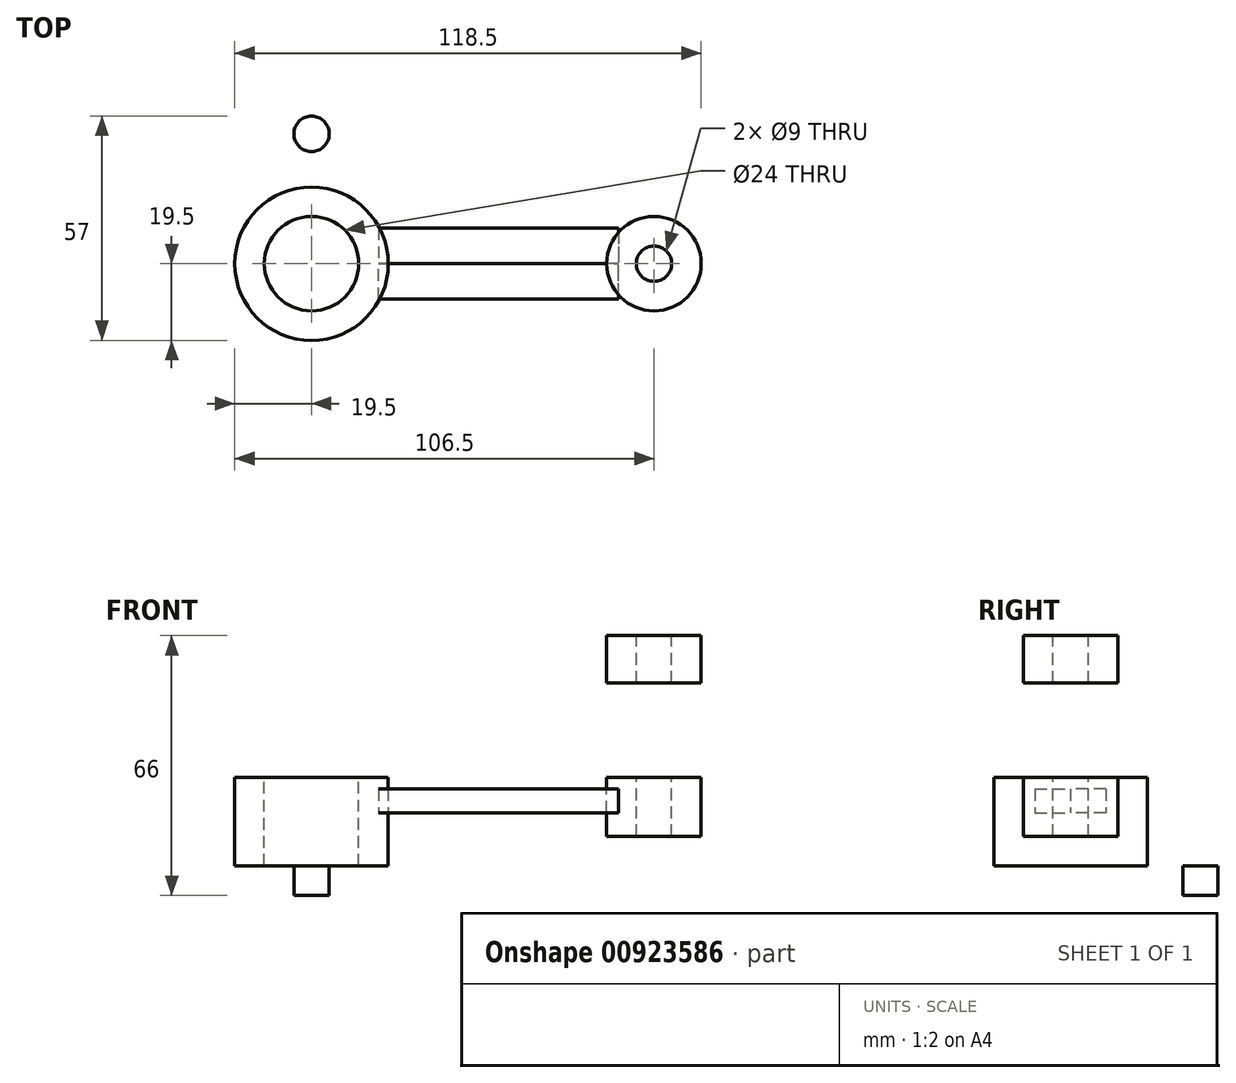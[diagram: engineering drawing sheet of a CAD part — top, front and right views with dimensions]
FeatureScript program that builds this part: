
annotation { "Feature Type Name" : "Feature", "Feature Type Description" : "" }
export const myFeature = defineFeature(function(context is Context, id is Id, definition is map)
    precondition{}
    {
        {
            var Q0;
            Q0=qCreatedBy(makeId("Top.planeOp"),FACE);
            var sketch = newSketch(context, id + "F0", { "sketchPlane" : qUnion([Q0])});
            skLineSegment(sketch, "E0.bottom", {"start": v(19.5, 45) * mm, "end": v(-19.5, 45) * mm});
            skLineSegment(sketch, "E0.top", {"start": v(19.5, -45) * mm, "end": v(-19.5, -45) * mm});
            skLineSegment(sketch, "E0.left", {"start": v(19.5, 45) * mm, "end": v(19.5, -45) * mm});
            skLineSegment(sketch, "E0.right", {"start": v(-19.5, 45) * mm, "end": v(-19.5, -45) * mm});
            skPoint(sketch, "E0.middle", {"position": v(0, 0) * mm});
            skSolve(sketch);
        }
        {
            var Q0;
            Q0=makeQuery(id+"F0.imprint","IMPRINT",FACE,{"disambiguationData":[TD([[makeQuery(id+"F0.imprint","IMPRINT",EDGE,{"derivedFrom":sQuery(id+"F0.wireOp",EDGE,"E0.bottom")}),1.0]])]});
            extrude(context, id + "F1", {"entities" : qUnion([Q0]), "depth" : 7.5 * mm, "offsetDistance" : 25 * mm});
        }
        {
            var Q0;
            Q0=makeQuery(id+"F1.opExtrude","CAP_FACE",FACE,{"disambiguationData":[OSD([sQuery(id+"F0.wireOp",EDGE,"E0.bottom"),sQuery(id+"F0.wireOp",EDGE,"E0.top"),sQuery(id+"F0.wireOp",EDGE,"E0.left"),sQuery(id+"F0.wireOp",EDGE,"E0.right")])],"isStart":false});
            var sketch = newSketch(context, id + "F2", { "sketchPlane" : qUnion([Q0])});
            skCircle(sketch, "E1", {"center": v(0, 0) * mm, "radius": 19.5 * mm});
            skSolve(sketch);
        }
        {
            var Q0;
            {var subQ0=sQuery(id+"F0.wireOp",EDGE,"E0.right");var subQ1=sQuery(id+"F0.wireOp",EDGE,"E0.left");var subQ2=sQuery(id+"F0.wireOp",EDGE,"E0.top");var subQ3=makeQuery(id+"F1.opExtrude","CAP_FACE",FACE,{"disambiguationData":[OSD([sQuery(id+"F0.wireOp",EDGE,"E0.bottom"),subQ2,subQ1,subQ0])],"isStart":false});Q0=makeQuery(id+"FBpe31tHuC7by74_1.boolean.opBoolean","SPLIT",FACE,{"disambiguationData":[TD([makeQuery(id+"F1.opExtrude","SWEPT_FACE",FACE,{"disambiguationData":[OSD([subQ2])]})])],"derivedFrom":subQ3});}
            var sketch = newSketch(context, id + "F3", { "sketchPlane" : qUnion([Q0])});
            skCircle(sketch, "E2", {"center": v(0, -33) * mm, "radius": 4.5 * mm});
            skCircle(sketch, "E3.MirrorC", {"center": v(0, 33) * mm, "radius": 4.5 * mm});
            skSolve(sketch);
        }
        {
            var Q0;
            Q0=makeQuery(id+"F3.imprint","IMPRINT",FACE,{"disambiguationData":[TD([[makeQuery(id+"F3.imprint","IMPRINT",EDGE,{"derivedFrom":sQuery(id+"F3.wireOp",EDGE,"E2")}),1.0]])]});
            var Q1;
            Q1=makeQuery(id+"F3.imprint","IMPRINT",FACE,{"disambiguationData":[TD([[makeQuery(id+"F3.imprint","IMPRINT",EDGE,{"derivedFrom":sQuery(id+"F3.wireOp",EDGE,"E3.MirrorC")}),-1.0]])]});
            var Q2;
            Q2=makeQuery(id+"F1.opExtrude","CAP_FACE",FACE,{"disambiguationData":[OSD([sQuery(id+"F0.wireOp",EDGE,"E0.bottom"),sQuery(id+"F0.wireOp",EDGE,"E0.top"),sQuery(id+"F0.wireOp",EDGE,"E0.left"),sQuery(id+"F0.wireOp",EDGE,"E0.right")])],"isStart":true});
            extrude(context, id + "F4", {"entities" : qUnion([Q0, Q1]), "operationType" : NewBodyOperationType.REMOVE, "endBound" : BoundingType.UP_TO_SURFACE, "oppositeDirection" : true, "depth" : 25 * mm, "endBoundEntityFace" : qUnion([Q2]), "offsetDistance" : 25 * mm});
        }
        {
            var Q0;
            {var subQ0=sQuery(id+"F2.wireOp",EDGE,"E1");var subQ1=makeQuery(id+"F2.imprint","INTERSECT",VERTEX,{"derivedFrom":[makeQuery(id+"F1.opExtrude","CAP_EDGE",EDGE,{"disambiguationData":[OSD([sQuery(id+"F0.wireOp",EDGE,"E0.left")])],"isStart":false}),subQ0]});Q0=makeQuery(id+"F2.imprint","IMPRINT",FACE,{"disambiguationData":[TD([[makeQuery(id+"F2.imprint","IMPRINT",EDGE,{"disambiguationData":[TD([[subQ1,-1.0]])],"derivedFrom":subQ0}),1.0]])]});}
            extrude(context, id + "F5", {"entities" : qUnion([Q0]), "operationType" : NewBodyOperationType.ADD, "depth" : 22.5 * mm, "offsetDistance" : 25 * mm});
        }
        {
            var Q0;
            Q0=makeQuery(id+"F5.opExtrude","CAP_FACE",FACE,{"disambiguationData":[OSD([sQuery(id+"F2.wireOp",EDGE,"E1")])],"isStart":false});
            var sketch = newSketch(context, id + "F6", { "sketchPlane" : qUnion([Q0])});
            skCircle(sketch, "E4", {"center": v(0, 0) * mm, "radius": 12 * mm});
            skSolve(sketch);
        }
        {
            var Q0;
            Q0=makeQuery(id+"F6.imprint","IMPRINT",FACE,{"disambiguationData":[TD([[makeQuery(id+"F6.imprint","IMPRINT",EDGE,{"derivedFrom":sQuery(id+"F6.wireOp",EDGE,"E4")}),1.0]])]});
            var Q1;
            Q1=makeQuery(id+"F1.opExtrude","CAP_FACE",FACE,{"disambiguationData":[OSD([sQuery(id+"F0.wireOp",EDGE,"E0.bottom"),sQuery(id+"F0.wireOp",EDGE,"E0.top"),sQuery(id+"F0.wireOp",EDGE,"E0.left"),sQuery(id+"F0.wireOp",EDGE,"E0.right")])],"isStart":true});
            extrude(context, id + "F7", {"entities" : qUnion([Q0]), "operationType" : NewBodyOperationType.REMOVE, "endBound" : BoundingType.UP_TO_SURFACE, "oppositeDirection" : true, "depth" : 25 * mm, "endBoundEntityFace" : qUnion([Q1]), "offsetDistance" : 25 * mm});
        }
        {
            var Q0;
            Q0=makeQuery(id+"F5.opExtrude","CAP_FACE",FACE,{"disambiguationData":[OSD([sQuery(id+"F2.wireOp",EDGE,"E1")])],"isStart":false});
            var sketch = newSketch(context, id + "F8", { "sketchPlane" : qUnion([Q0])});
            skCircle(sketch, "E5", {"center": v(87, 0) * mm, "radius": 12 * mm});
            skSolve(sketch);
        }
        {
            var Q0;
            Q0=makeQuery(id+"F8.imprint","IMPRINT",FACE,{"disambiguationData":[TD([[makeQuery(id+"F8.imprint","IMPRINT",EDGE,{"derivedFrom":sQuery(id+"F8.wireOp",EDGE,"E5")}),1.0]])]});
            extrude(context, id + "F9", {"entities" : qUnion([Q0]), "oppositeDirection" : true, "depth" : 15 * mm, "offsetDistance" : 25 * mm});
        }
        {
            var Q0;
            Q0=qCreatedBy(makeId("Front.planeOp"),FACE);
            var sketch = newSketch(context, id + "F10", { "sketchPlane" : qUnion([Q0])});
            skLineSegment(sketch, "E6", {"start": v(87, 66) * mm, "end": v(87, 54) * mm});
            skLineSegment(sketch, "E7", {"start": v(87, 54) * mm, "end": v(99, 54) * mm});
            skLineSegment(sketch, "E8", {"start": v(99, 54) * mm, "end": v(99, 66) * mm});
            skLineSegment(sketch, "E9", {"start": v(99, 66) * mm, "end": v(87, 66) * mm});
            skSolve(sketch);
        }
        {
            var Q0;
            Q0=makeQuery(id+"F10.imprint","IMPRINT",FACE,{"disambiguationData":[TD([[makeQuery(id+"F10.imprint","IMPRINT",EDGE,{"derivedFrom":sQuery(id+"F10.wireOp",EDGE,"E6")}),1.0]])]});
            var Q1;
            Q1=sQuery(id+"F10.wireOp",EDGE,"E6");
            revolve(context, id + "F11", {"surfaceOperationType" : NewSurfaceOperationType.NEW, "entities" : qUnion([Q0]), "axis" : qUnion([Q1]), "revolveType" : RevolveType.FULL});
        }
        {
            var Q0;
            Q0=makeQuery(id+"F11.opRevolve","SWEPT_FACE",FACE,{"disambiguationData":[OSD([sQuery(id+"F10.wireOp",EDGE,"E9")])]});
            var sketch = newSketch(context, id + "F12", { "sketchPlane" : qUnion([Q0])});
            skCircle(sketch, "E10", {"center": v(87, 0) * mm, "radius": 4.5 * mm});
            skSolve(sketch);
        }
        {
            var Q0;
            Q0=makeQuery(id+"F12.imprint","IMPRINT",FACE,{"disambiguationData":[TD([[makeQuery(id+"F12.imprint","IMPRINT",EDGE,{"derivedFrom":sQuery(id+"F12.wireOp",EDGE,"E10")}),1.0]])]});
            var Q1;
            Q1=makeQuery(id+"F9.opExtrude","CAP_FACE",FACE,{"disambiguationData":[OSD([sQuery(id+"F8.wireOp",EDGE,"E5")])],"isStart":false});
            var Q2;
            Q2=makeQuery(id+"F9.opExtrude","SWEPT_BODY",BODY,{"disambiguationData":[OSD([sQuery(id+"F8.wireOp",EDGE,"E5")])]});
            extrude(context, id + "F13", {"entities" : qUnion([Q0]), "operationType" : NewBodyOperationType.REMOVE, "endBound" : BoundingType.UP_TO_SURFACE, "oppositeDirection" : true, "depth" : 25 * mm, "endBoundEntityFace" : qUnion([Q1]), "endBoundEntityBody" : qUnion([Q2]), "offsetDistance" : 25 * mm});
        }
        {
            var Q0;
            Q0=makeQuery(id+"F9.opExtrude","CAP_FACE",FACE,{"disambiguationData":[OSD([sQuery(id+"F8.wireOp",EDGE,"E5")])],"isStart":true});
            var sketch = newSketch(context, id + "F14", { "sketchPlane" : qUnion([Q0])});
            skCircle(sketch, "E11", {"center": v(87, 0) * mm, "radius": 4.5 * mm});
            skSolve(sketch);
        }
        {
            var Q0;
            Q0=makeQuery(id+"F14.imprint","IMPRINT",FACE,{"disambiguationData":[TD([[makeQuery(id+"F14.imprint","IMPRINT",EDGE,{"derivedFrom":sQuery(id+"F14.wireOp",EDGE,"E11")}),1.0]])]});
            var Q1;
            Q1=makeQuery(id+"F9.opExtrude","CAP_FACE",FACE,{"disambiguationData":[OSD([sQuery(id+"F8.wireOp",EDGE,"E5")])],"isStart":false});
            extrude(context, id + "F15", {"entities" : qUnion([Q0]), "operationType" : NewBodyOperationType.REMOVE, "endBound" : BoundingType.UP_TO_SURFACE, "oppositeDirection" : true, "depth" : 25 * mm, "endBoundEntityFace" : qUnion([Q1]), "offsetDistance" : 25 * mm});
        }
        {
            var Q0;
            Q0=qCreatedBy(makeId("Front.planeOp"),FACE);
            var sketch = newSketch(context, id + "F16", { "sketchPlane" : qUnion([Q0])});
            skLineSegment(sketch, "E12", {"start": v(17, 27) * mm, "end": v(17, 21) * mm});
            skLineSegment(sketch, "E13", {"start": v(17, 21) * mm, "end": v(78, 21) * mm});
            skLineSegment(sketch, "E14", {"start": v(78, 21) * mm, "end": v(78, 27) * mm});
            skLineSegment(sketch, "E15", {"start": v(78, 27) * mm, "end": v(17, 27) * mm});
            skSolve(sketch);
        }
        {
            var Q0;
            Q0=makeQuery(id+"F16.imprint","IMPRINT",FACE,{"disambiguationData":[TD([[makeQuery(id+"F16.imprint","IMPRINT",EDGE,{"derivedFrom":sQuery(id+"F16.wireOp",EDGE,"E12")}),1.0]])]});
            extrude(context, id + "F17", {"entities" : qUnion([Q0]), "depth" : 9 * mm, "offsetDistance" : 25 * mm});
        }
        {
            var Q0;
            Q0=makeQuery(id+"F17.opExtrude","SWEPT_BODY",BODY,{"disambiguationData":[OSD([sQuery(id+"F16.wireOp",EDGE,"E12"),sQuery(id+"F16.wireOp",EDGE,"E13"),sQuery(id+"F16.wireOp",EDGE,"E14"),sQuery(id+"F16.wireOp",EDGE,"E15")])]});
            var Q1;
            Q1=qCreatedBy(makeId("Front.planeOp"),FACE);
            mirror(context, id + "F18", {"entities" : qUnion([Q0]), "mirrorPlane" : qUnion([Q1])});
        }
    });
